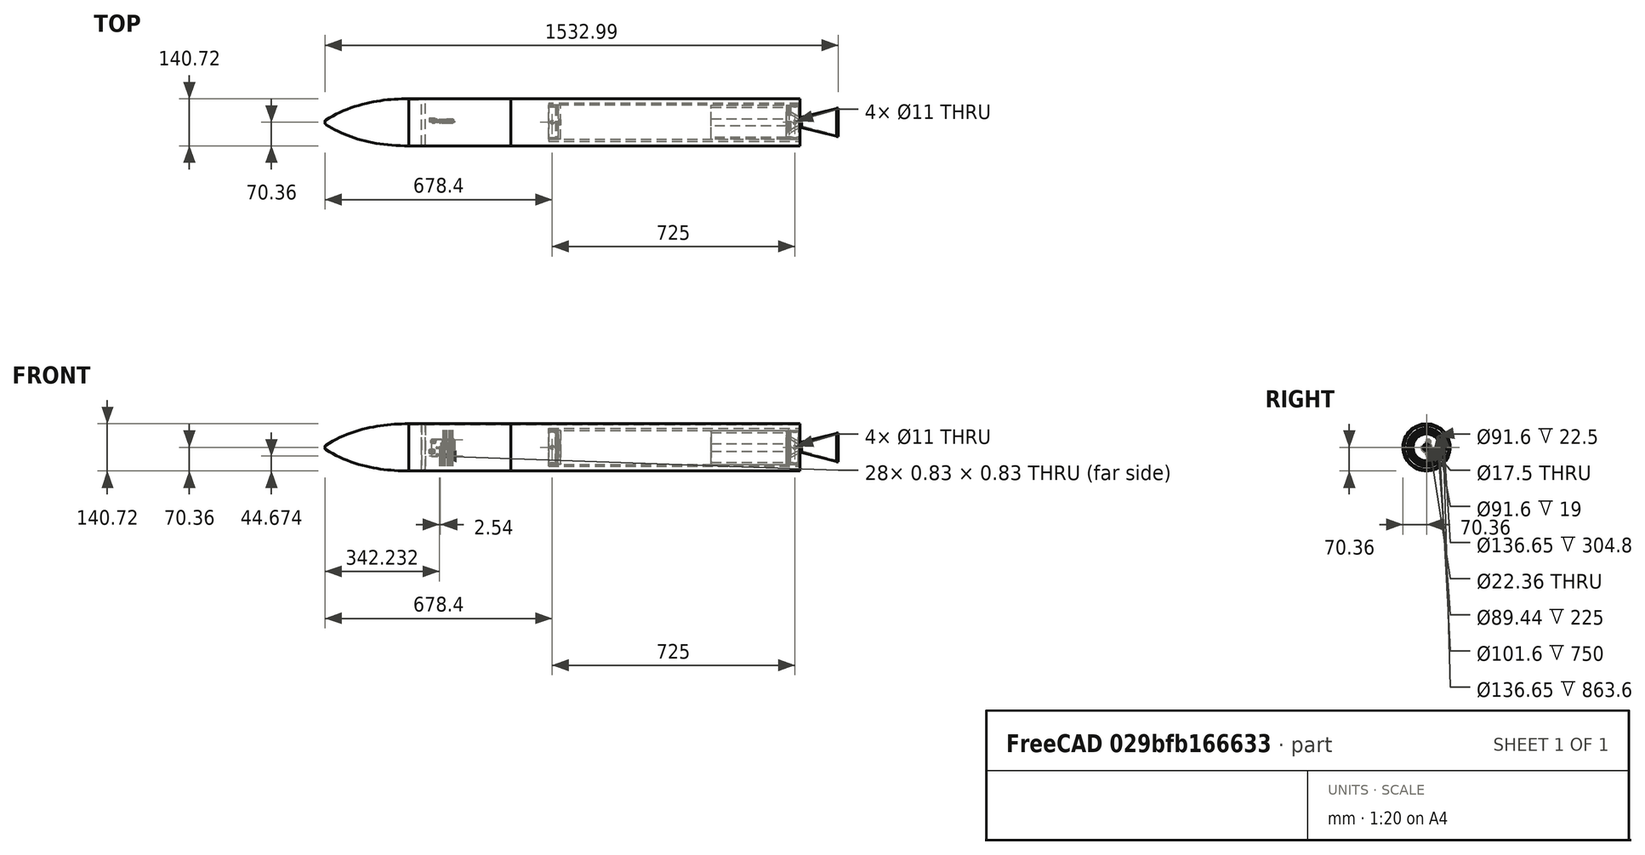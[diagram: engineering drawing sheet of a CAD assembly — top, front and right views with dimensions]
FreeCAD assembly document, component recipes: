
FREECAD ASSEMBLY — COMPONENT RECIPES ("rocket3")

This assembly document has 6 components, labeled P0..P5 below (a component is one placed body or linked part). 5 of them carry a construction recipe — the FreeCAD feature program that regenerates the part from scratch, quoted from this document or its linked companion documents; the rest are supplied as boundary geometry only. No exploded tour is included for this assembly.
COMPONENT P0 — geometry summary ("motor"; no construction recipe available for this part):
  bounding box: 829.6 x 101.6 x 101.6 mm
  tessellated surface: 440 triangles
  volume: 72218000565824792557368503203952325115086539148152444708673987785426709532794152812544 mm^3 (843319523379228956511091711220987211008015818571882914169777494254398885213503488% of its bounding box)
  symmetry: 4-fold rotationally symmetric about the x axis; mirror-symmetric across its y mid-plane, z mid-plane
COMPONENT P1 — recipe-attached ("FuelSegment", modeled in this document).
Construction recipe (the document's own serialized feature program — sketch geometry with constraints, then the solid features built on it; lengths are millimeters unless a unit is written):

FEATURE [Sketcher::SketchObject] Sketch008
  FullyConstrained = true
  MapMode = 5
  Placement = pos=(-40,0,0) rot=(0.57735,-0.57735,-0.57735;2.0944rad)
  Support = -> [DatumPlane002]
  expr: Constraints[3] = Spreadsheet.D13
  expr: Constraints[1] = Spreadsheet.B13
  sketch-geometry (2):
    g0: Circle CenterX=0 CenterY=0 CenterZ=0 NormalX=0 NormalY=0 NormalZ=1 AngleXU=0 Radius=50.8
    g1: Circle CenterX=0 CenterY=0 CenterZ=0 NormalX=0 NormalY=0 NormalZ=1 AngleXU=0 Radius=44.72
  constraints (4):
    c: Coincident(g0,g-1)
    c: Radius(g0) = 50.8
    c: Coincident(g1,g0)
    c: Radius(g1) = 44.72
FEATURE [PartDesign::Pad] Pad001
  Direction = (1,1,1)
  Length = 225
  Length2 = 100
  Placement = pos=(-40,0,0) rot=(0.57735,-0.57735,-0.57735;2.0944rad)
  Profile = -> Sketch008
  Type = 0
  expr: Length = Spreadsheet.B20
FEATURE [PartDesign::Body] Body003  label="pvc"
  Group = -> [Sketch008,Pad001]
  Origin = -> Origin008
  Tip = -> Pad001
FEATURE [Sketcher::SketchObject] Sketch009
  FullyConstrained = true
  MapMode = 5
  Placement = pos=(-40,0,0) rot=(0.57735,-0.57735,-0.57735;2.0944rad)
  Support = -> [DatumPlane002]
  expr: Constraints[3] = Spreadsheet.D13 / 4
  expr: Constraints[1] = Spreadsheet.D13
  sketch-geometry (2):
    g0: Circle CenterX=0 CenterY=0 CenterZ=0 NormalX=0 NormalY=0 NormalZ=1 AngleXU=0 Radius=44.72
    g1: Circle CenterX=0 CenterY=0 CenterZ=0 NormalX=0 NormalY=0 NormalZ=1 AngleXU=0 Radius=11.18
  constraints (4):
    c: Coincident(g0,g-1)
    c: Radius(g0) = 44.72
    c: Coincident(g1,g0)
    c: Radius(g1) = 11.18
FEATURE [PartDesign::Pad] Pad002
  Direction = (1,1,1)
  Length = 225
  Length2 = 100
  Placement = pos=(-40,0,0) rot=(0.57735,-0.57735,-0.57735;2.0944rad)
  Profile = -> Sketch009
  Type = 0
  expr: Length = Spreadsheet.B20
FEATURE [PartDesign::Body] Body004  label="fuel"
  Group = -> [Sketch009,Pad002]
  Origin = -> Origin009
  Tip = -> Pad002
COMPONENT P2 — recipe-attached ("NoseCone", modeled in this document).
Construction recipe (the document's own serialized feature program — sketch geometry with constraints, then the solid features built on it; lengths are millimeters unless a unit is written):

FEATURE [PartDesign::CoordinateSystem] LCS_0004
  AttacherType = Attacher::AttachEngine3D
  MapMode = 2
  Support = -> [X_Axis014]
FEATURE [Sketcher::SketchObject] Sketch012
  FullyConstrained = false
  MapMode = 5
  Support = -> [XY_Plane014]
  expr: Constraints[18] = Spreadsheet.G10 * 0.6
  expr: Constraints[6] = Spreadsheet.E9 + Spreadsheet.E11
  expr: Constraints[5] = Spreadsheet.G10
  expr: Constraints[32] = Spreadsheet.E11
  expr: Constraints[3] = Spreadsheet.G8 + Spreadsheet.G9
  sketch-geometry (13):
    g0: LineSegment StartX=-1168.4 StartY=0 StartZ=0 EndX=-1418.4 EndY=0 EndZ=0
    g1: LineSegment StartX=-1168.4 StartY=0 StartZ=0 EndX=-1168.4 EndY=-70.358 EndZ=0
    g2: Circle CenterX=-1168.4 CenterY=-70.358 CenterZ=0 NormalX=0 NormalY=0 NormalZ=1 AngleXU=0 Radius=1
    g3: Circle CenterX=-1318.4 CenterY=-70.358 CenterZ=0 NormalX=0 NormalY=0 NormalZ=1 AngleXU=0 Radius=1
    g4: Circle CenterX=-1418.4 CenterY=-5 CenterZ=0 NormalX=0 NormalY=0 NormalZ=1 AngleXU=0 Radius=1
    g5: BSplineCurve PolesCount=3 KnotsCount=2 Degree=2 IsPeriodic=0
    g6: GeomPoint X=-1168.4 Y=-70.358 Z=0
    g7: GeomPoint X=-1418.4 Y=-5 Z=0
    g8: LineSegment StartX=-1418.4 StartY=-5 StartZ=0 EndX=-1418.4 EndY=0 EndZ=0
    g9: LineSegment StartX=-1168.4 StartY=-70.358 StartZ=0 EndX=-1168.4 EndY=-68.326 EndZ=0
    g10: LineSegment StartX=-1168.4 StartY=-68.326 StartZ=0 EndX=-1118.4 EndY=-68.326 EndZ=0
    g11: LineSegment StartX=-1168.4 StartY=0 StartZ=0 EndX=-1118.4 EndY=0 EndZ=0
    g12: LineSegment StartX=-1118.4 StartY=-68.326 StartZ=0 EndX=-1118.4 EndY=0 EndZ=0
  constraints (33):
    c: Horizontal(g0)
    c: Coincident(g1,g0)
    c: Vertical(g1)
    c: DistanceX(g1,g-1) = 1168.4
    c: PointOnObject(g0,g-1)
    c: DistanceX(g0,g0) = 250
    c: DistanceY(g1,g1) = 70.358
    c: Coincident(g5,g1)
    c: Weight(g2) = 1
    c: Equal(g2,g3)
    c: Equal(g2,g4)
    c: InternalAlignment(g2,g5)
    c: InternalAlignment(g3,g5)
    c: InternalAlignment(g4,g5)
    c: InternalAlignment(g6,g5)
    c: InternalAlignment(g7,g5)
    c: Vertical(g5,g0)
    c: Horizontal(g5,g3)
    c: DistanceX(g3,g5) = 150
    c: DistanceY(g5,g0) = 5
    c: Coincident(g8,g5)
    c: Coincident(g8,g0)
    c: Coincident(g9,g5)
    c: PointOnObject(g9,g1)
    c: Coincident(g10,g9)
    c: Horizontal(g10)
    c: PointOnObject(g11,g-1)
    c: Horizontal(g11)
    c: Coincident(g12,g10)
    c: Coincident(g12,g11)
    c: Vertical(g12)
    c: DistanceX(g10,g10) = 50
    c: DistanceY(g9,g9) = 2.032
FEATURE [PartDesign::Revolution] Revolution003
  Angle = 360
  Axis = (1,0,0)
  Base = (0,0,0)
  Profile = -> Sketch012
  ReferenceAxis = -> X_Axis014
  Reversed = true
FEATURE [PartDesign::Chamfer] Chamfer
  Angle = 10
  Base = -> Revolution003 [Edge5]
  BaseFeature = -> Revolution003
  ChamferType = 2
  FlipDirection = false
  Size = 12
  Size2 = 1
  SupportTransform = false
FEATURE [PartDesign::Fillet] Fillet003
  Base = -> Chamfer [Edge7]
  BaseFeature = -> Chamfer
  Radius = 5
  SupportTransform = false
FEATURE [PartDesign::Body] Cone
  Group = -> [LCS_0004,Sketch012,Revolution003,Chamfer,Fillet003]
  Origin = -> Origin014
  Tip = -> Fillet003
COMPONENT P3 — recipe-attached ("OuterTube", modeled in this document).
Construction recipe (the document's own serialized feature program — sketch geometry with constraints, then the solid features built on it; lengths are millimeters unless a unit is written):

FEATURE [Sketcher::SketchObject] Sketch010
  FullyConstrained = true
  MapMode = 5
  Placement = pos=(0,0,0) rot=(0.57735,0.57735,0.57735;2.0944rad)
  Support = -> [YZ_Plane011]
  expr: Constraints[3] = Spreadsheet.E9 + Spreadsheet.E11
  expr: Constraints[2] = Spreadsheet.E9
  sketch-geometry (2):
    g0: Circle CenterX=0 CenterY=0 CenterZ=0 NormalX=0 NormalY=0 NormalZ=1 AngleXU=0 Radius=68.326
    g1: Circle CenterX=0 CenterY=0 CenterZ=0 NormalX=0 NormalY=0 NormalZ=1 AngleXU=0 Radius=70.358
  constraints (4):
    c: Coincident(g0,g-1)
    c: Coincident(g1,g0)
    c: Radius(g0) = 68.326
    c: Radius(g1) = 70.358
FEATURE [PartDesign::Pad] Pad003
  Direction = (1,1,1)
  Length = 863.6
  Length2 = 100
  Placement = pos=(0,0,0) rot=(0.57735,0.57735,0.57735;2.0944rad)
  Profile = -> Sketch010
  Reversed = true
  Type = 0
  expr: Length = Spreadsheet.G8
FEATURE [PartDesign::Body] Body005  label="BottomTube"
  Group = -> [Sketch010,Pad003]
  Origin = -> Origin011
  Tip = -> Pad003
FEATURE [PartDesign::Plane] DatumPlane003
  Length = 168.312
  MapMode = 5
  Placement = pos=(-863.6,3.835e-13,-2.876e-13) rot=(0.57735,0.57735,-0.57735;4.18879rad)
  ResizeMode = 0
  Support = -> [Pad003]
  Width = 168.55
FEATURE [Sketcher::SketchObject] Sketch011
  FullyConstrained = true
  MapMode = 5
  Placement = pos=(-863.6,3.835e-13,-2.876e-13) rot=(-0.57735,-0.57735,0.57735;2.0944rad)
  Support = -> [DatumPlane003]
  expr: Constraints[3] = Spreadsheet.E9 + Spreadsheet.E11
  expr: Constraints[2] = Spreadsheet.E9
  sketch-geometry (2):
    g0: Circle CenterX=0 CenterY=0 CenterZ=0 NormalX=0 NormalY=0 NormalZ=1 AngleXU=0 Radius=68.326
    g1: Circle CenterX=0 CenterY=0 CenterZ=0 NormalX=0 NormalY=0 NormalZ=1 AngleXU=0 Radius=70.358
  constraints (4):
    c: Coincident(g0,g-1)
    c: Coincident(g1,g0)
    c: Radius(g0) = 68.326
    c: Radius(g1) = 70.358
FEATURE [PartDesign::Pad] Pad004
  Direction = (1,1,1)
  Length = 304.8
  Length2 = 100
  Placement = pos=(-863.6,3.835e-13,-2.876e-13) rot=(0.57735,0.57735,-0.57735;4.18879rad)
  Profile = -> Sketch011
  Type = 0
  expr: Length = Spreadsheet.G9
FEATURE [PartDesign::Body] Body006  label="TopTube"
  Group = -> [DatumPlane003,Sketch011,Pad004]
  Origin = -> Origin012
  Tip = -> Pad004
COMPONENT P4 — recipe-attached ("casing", modeled in this document).
Construction recipe (the document's own serialized feature program — sketch geometry with constraints, then the solid features built on it; lengths are millimeters unless a unit is written):

FEATURE [Sketcher::SketchObject] Sketch003
  FullyConstrained = true
  MapMode = 5
  Placement = pos=(0,0,0) rot=(0.57735,0.57735,0.57735;2.0944rad)
  Support = -> [YZ_Plane004]
  expr: Constraints[3] = Spreadsheet.B13 + Spreadsheet.B16
  expr: Constraints[1] = Spreadsheet.B13
  sketch-geometry (2):
    g0: Circle CenterX=0 CenterY=0 CenterZ=0 NormalX=0 NormalY=0 NormalZ=1 AngleXU=0 Radius=50.8
    g1: Circle CenterX=0 CenterY=0 CenterZ=0 NormalX=0 NormalY=0 NormalZ=1 AngleXU=0 Radius=56.8
  constraints (4):
    c: Coincident(g0,g-1)
    c: Radius(g0) = 50.8
    c: Coincident(g1,g0)
    c: Radius(g1) = 56.8
FEATURE [PartDesign::Pad] Pad
  Direction = (1,1,1)
  Length = 750
  Length2 = 100
  Placement = pos=(0,0,0) rot=(0.57735,0.57735,0.57735;2.0944rad)
  Profile = -> Sketch003
  Reversed = true
  Type = 0
  expr: Length = Spreadsheet.B19
FEATURE [PartDesign::Body] Body001
  Group = -> [Sketch003,Pad]
  Origin = -> Origin004
  Tip = -> Pad
COMPONENT P5 — recipe-attached ("bulkhead", modeled in this document).
Construction recipe (the document's own serialized feature program — sketch geometry with constraints, then the solid features built on it; lengths are millimeters unless a unit is written):

FEATURE [Sketcher::SketchObject] Sketch005
  FullyConstrained = true
  MapMode = 3
  Placement = pos=(0,0,0) rot=(1,0,0;3.14159rad)
  Support = -> [XZ_Plane006]
  expr: Constraints[17] = Spreadsheet.B19
  expr: Constraints[15] = Spreadsheet.B16
  expr: Constraints[11] = Spreadsheet.B13
  sketch-geometry (6):
    g0: LineSegment StartX=-715 StartY=50.8 StartZ=0 EndX=-715 EndY=0 EndZ=0
    g1: LineSegment StartX=-715 StartY=50.8 StartZ=0 EndX=-750 EndY=50.8 EndZ=0
    g2: LineSegment StartX=-750 StartY=45.8 StartZ=0 EndX=-721 EndY=45.8 EndZ=0
    g3: LineSegment StartX=-721 StartY=0 StartZ=0 EndX=-715 EndY=0 EndZ=0
    g4: LineSegment StartX=-721 StartY=0 StartZ=0 EndX=-721 EndY=45.8 EndZ=0
    g5: LineSegment StartX=-750 StartY=50.8 StartZ=0 EndX=-750 EndY=45.8 EndZ=0
  constraints (18):
    c: Vertical(g0)
    c: Coincident(g1,g0)
    c: Horizontal(g1)
    c: Horizontal(g2)
    c: PointOnObject(g3,g-1)
    c: Coincident(g3,g0)
    c: Coincident(g4,g3)
    c: Coincident(g4,g2)
    c: Vertical(g4)
    c: Coincident(g5,g1)
    c: Coincident(g5,g2)
    c: DistanceY(g0,g0) = 50.8
    c: PointOnObject(g0,g-1)
    c: Vertical(g5)
    c: DistanceY(g5,g5) = 5
    c: DistanceX(g3,g0) = 6
    c: DistanceX(g1,g0) = 35
    c: DistanceX(g1,g-1) = 750
FEATURE [PartDesign::Revolution] Revolution002
  Angle = 360
  Axis = (1,0,0)
  Base = (0,0,0)
  Placement = pos=(0,0,0) rot=(1,0,0;1.5708rad)
  Profile = -> Sketch005
  ReferenceAxis = -> X_Axis006
FEATURE [PartDesign::Fillet] Fillet002
  Base = -> Revolution002 [Face3]
  BaseFeature = -> Revolution002
  Placement = pos=(0,0,0) rot=(1,0,0;1.5708rad)
  Radius = 10
  SupportTransform = false
FEATURE [PartDesign::Hole] Hole001
  BaseFeature = -> Fillet002
  Depth = 25
  DepthType = 0
  Diameter = 17.5
  DrillForDepth = false
  DrillPoint = 1
  DrillPointAngle = 118
  HoleCutCountersinkAngle = 90
  HoleCutCustomValues = false
  HoleCutDepth = 0
  HoleCutDiameter = 6.1
  HoleCutType = 0
  ModelActualThread = false
  Placement = pos=(0,0,0) rot=(1,0,0;1.5708rad)
  Profile = -> Fillet002 [Face6]
  Tapered = false
  TaperedAngle = 90
  ThreadAngle = 0
  ThreadClass = 0
  ThreadCutOffInner = 0
  ThreadCutOffOuter = 0
  ThreadDirection = 0
  ThreadFit = 0
  ThreadPitch = 0
  ThreadSize = 22
  ThreadType = 1
  Threaded = false
FEATURE [Sketcher::SketchObject] Sketch006
  FullyConstrained = true
  MapMode = 5
  Support = -> [XY_Plane006]
  expr: Constraints[25] = 5 + Spreadsheet.E6 / 2
  expr: Constraints[24] = Spreadsheet.B19
  expr: Constraints[23] = Spreadsheet.B13
  expr: Constraints[19] = Spreadsheet.E6 * 0.4
  expr: Constraints[18] = Spreadsheet.E6
  sketch-geometry (9):
    g0: LineSegment StartX=-724 StartY=50 StartZ=0 EndX=-722 EndY=50 EndZ=0
    g1: LineSegment StartX=-722 StartY=50 StartZ=0 EndX=-722 EndY=50.8 EndZ=0
    g2: LineSegment StartX=-722 StartY=50.8 StartZ=0 EndX=-724 EndY=50.8 EndZ=0
    g3: LineSegment StartX=-724 StartY=50.8 StartZ=0 EndX=-724 EndY=50 EndZ=0
    g4: LineSegment StartX=-728 StartY=50.8 StartZ=0 EndX=-730 EndY=50.8 EndZ=0
    g5: LineSegment StartX=-730 StartY=50.8 StartZ=0 EndX=-730 EndY=50 EndZ=0
    g6: LineSegment StartX=-730 StartY=50 StartZ=0 EndX=-728 EndY=50 EndZ=0
    g7: LineSegment StartX=-728 StartY=50 StartZ=0 EndX=-728 EndY=50.8 EndZ=0
    g8: LineSegment StartX=-750 StartY=50.8 StartZ=0 EndX=-750 EndY=0 EndZ=0
  constraints (28):
    c: Coincident(g0,g1)
    c: Coincident(g1,g2)
    c: Coincident(g2,g3)
    c: Coincident(g3,g0)
    c: Horizontal(g0)
    c: Horizontal(g2)
    c: Vertical(g1)
    c: Vertical(g3)
    c: Coincident(g4,g5)
    c: Coincident(g5,g6)
    c: Coincident(g6,g7)
    c: Coincident(g7,g4)
    c: Horizontal(g4)
    c: Horizontal(g6)
    c: Vertical(g5)
    c: Vertical(g7)
    c: PointOnObject(g2,g4)
    c: Equal(g4,g2)
    c: DistanceX(g2,g1) = 2
    c: DistanceY(g1,g1) = 0.8
    c: PointOnObject(g6,g0)
    c: Vertical(g8)
    c: PointOnObject(g8,g-1)
    c: DistanceY(g8,g8) = 50.8
    c: DistanceX(g8,g-1) = 750
    c: DistanceX(g4,g1) = 6
    c: PointOnObject(g8,g4)
    c: DistanceX(g8,g4) = 20
FEATURE [PartDesign::Groove] Groove001
  Angle = 360
  Axis = (1,0,0)
  Base = (0,0,0)
  BaseFeature = -> Hole001
  Placement = pos=(0,0,0) rot=(1,0,0;1.5708rad)
  Profile = -> Sketch006
  ReferenceAxis = -> X_Axis006
  Reversed = true
FEATURE [Sketcher::SketchObject] Sketch007
  FullyConstrained = true
  MapMode = 5
  Placement = pos=(0,0,0) rot=(1,0,0;1.5708rad)
  Support = -> [XZ_Plane006]
  expr: Constraints[2] = Spreadsheet.B19 - Spreadsheet.E4 / 2 - 5
  expr: Constraints[1] = Spreadsheet.E4 / 2
  sketch-geometry (1):
    g0: Circle CenterX=-740 CenterY=0 CenterZ=0 NormalX=0 NormalY=0 NormalZ=1 AngleXU=0 Radius=5
  constraints (3):
    c: PointOnObject(g0,g-1)
    c: Radius(g0) = 5
    c: DistanceX(g0,g-1) = 740
FEATURE [PartDesign::Hole] Hole002
  BaseFeature = -> Groove001
  Depth = 25
  DepthType = 1
  Diameter = 11
  DrillForDepth = false
  DrillPoint = 1
  DrillPointAngle = 118
  HoleCutCountersinkAngle = 90
  HoleCutCustomValues = false
  HoleCutDepth = 0
  HoleCutDiameter = 6.1
  HoleCutType = 0
  ModelActualThread = false
  Placement = pos=(0,0,0) rot=(1,0,0;1.5708rad)
  Profile = -> Sketch007
  Tapered = false
  TaperedAngle = 90
  ThreadAngle = 0
  ThreadClass = 0
  ThreadCutOffInner = 0
  ThreadCutOffOuter = 0
  ThreadDirection = 0
  ThreadFit = 0
  ThreadPitch = 0
  ThreadSize = 18
  ThreadType = 1
  Threaded = false
FEATURE [PartDesign::PolarPattern] PolarPattern001
  Angle = 360
  Axis = -> X_Axis006
  BaseFeature = -> Hole002
  Occurrences = 4
  Originals = -> [Hole002]
  Placement = pos=(0,0,0) rot=(1,0,0;1.5708rad)
FEATURE [PartDesign::Body] Body002
  Group = -> [Sketch005,Revolution002,Fillet002,Hole001,Sketch006,Groove001,Sketch007,Hole002,PolarPattern001]
  Origin = -> Origin006
  Tip = -> PolarPattern001
PROVENANCE & LICENSES
A FreeCAD (.FCStd) document from a public repository crawl; recipes are the document's own serialized feature recipes (and, for linked parts, companion documents' recipes).
License: as declared in the source repository (recorded in the dataset sidecar).
